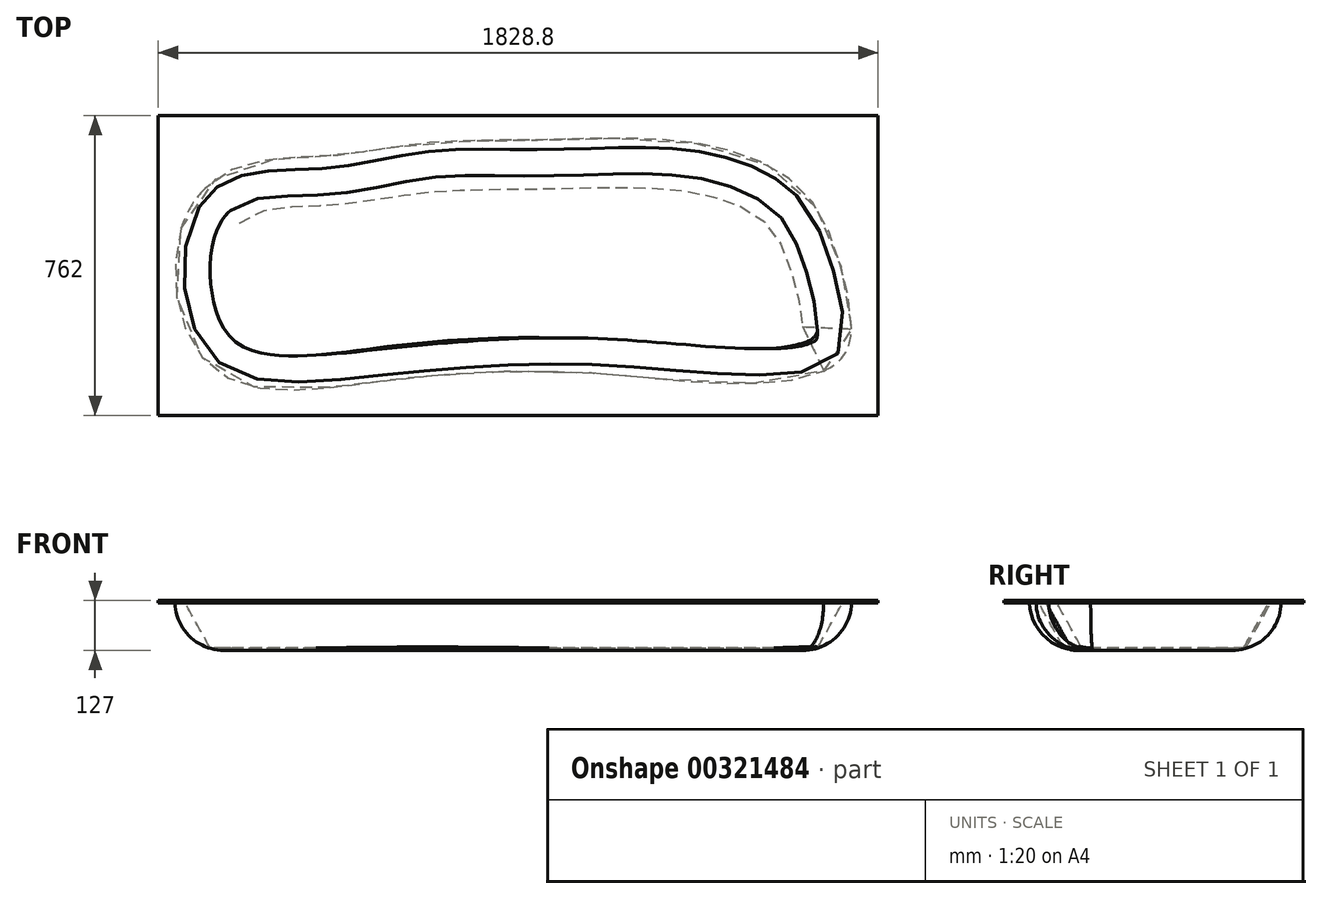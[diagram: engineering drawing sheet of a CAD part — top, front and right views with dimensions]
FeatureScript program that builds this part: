
annotation { "Feature Type Name" : "Feature", "Feature Type Description" : "" }
export const myFeature = defineFeature(function(context is Context, id is Id, definition is map)
    precondition{}
    {
        {
            var Q0;
            Q0=qCreatedBy(makeId("Top.planeOp"),FACE);
            var sketch = newSketch(context, id + "F0", { "sketchPlane" : qUnion([Q0])});
            skLineSegment(sketch, "E0.bottom", {"start": v(-1740.96, 737.08) * mm, "end": v(87.84, 737.08) * mm});
            skLineSegment(sketch, "E0.top", {"start": v(-1740.96, -24.92) * mm, "end": v(87.84, -24.92) * mm});
            skLineSegment(sketch, "E0.left", {"start": v(-1740.96, 737.08) * mm, "end": v(-1740.96, -24.92) * mm});
            skLineSegment(sketch, "E0.right", {"start": v(87.84, 737.08) * mm, "end": v(87.84, -24.92) * mm});
            skFitSpline(sketch, "E1", {"points": [v(-1683.24, 449.86) * mm, v(-1541.71, 604.65) * mm, v(-1298.47, 635.6) * mm, v(-1064.08, 666.57) * mm, v(-758.92, 675.41) * mm, v(-374.16, 666.57) * mm, v(-104.38, 547.16) * mm, v(0, 326.03) * mm, v(0, 127.01) * mm, v(-241.48, 56.25) * mm, v(-639.51, 82.79) * mm, v(-1112.73, 69.52) * mm, v(-1497.49, 47.4) * mm, v(-1661.12, 171.24) * mm, v(-1683.24, 449.86) * mm]});
            skFitSpline(sketch, "E2", {"points": [v(-1643.63, 182.8) * mm, v(-1661.97, 449.86) * mm, v(-1541.71, 580.79) * mm, v(-1297, 604.65) * mm, v(-1062.24, 644.98) * mm, v(-754.12, 650.48) * mm, v(-378.14, 646.81) * mm, v(-119.54, 533.1) * mm, v(-18.67, 314.85) * mm, v(-18.67, 127.01) * mm, v(-246.1, 78.26) * mm, v(-639.51, 103.94) * mm, v(-1120.93, 82.79) * mm, v(-1497.49, 69.1) * mm, v(-1643.63, 182.8) * mm]});
            skSolve(sketch);
        }
        {
            var Q0;
            Q0=makeQuery(id+"F0.imprint","IMPRINT",FACE,{"disambiguationData":[TD([[makeQuery(id+"F0.imprint","IMPRINT",EDGE,{"derivedFrom":sQuery(id+"F0.wireOp",EDGE,"E1")}),-1.0]])]});
            var Q1;
            Q1=makeQuery(id+"F0.imprint","IMPRINT",FACE,{"disambiguationData":[TD([[makeQuery(id+"F0.imprint","IMPRINT",EDGE,{"derivedFrom":sQuery(id+"F0.wireOp",EDGE,"E2")}),-1.0]])]});
            extrude(context, id + "F1", {"entities" : qUnion([Q0, Q1]), "oppositeDirection" : true, "depth" : 127 * mm});
        }
        {
            var Q0;
            Q0=makeQuery(id+"F1.opExtrude","CAP_EDGE",EDGE,{"disambiguationData":[OSD([sQuery(id+"F0.wireOp",EDGE,"E1")])],"isStart":false});
            fillet(context, id + "F2", {"entities" : qUnion([Q0]), "radius" : 124.46 * mm, "tangentPropagation" : true, "allowEdgeOverflow" : false});
        }
        {
            var Q0;
            Q0=makeQuery(id+"F0.imprint","IMPRINT",FACE,{"disambiguationData":[TD([[makeQuery(id+"F0.imprint","IMPRINT",EDGE,{"derivedFrom":sQuery(id+"F0.wireOp",EDGE,"E0.bottom")}),-1.0]])]});
            extrude(context, id + "F3", {"entities" : qUnion([Q0]), "operationType" : NewBodyOperationType.ADD, "oppositeDirection" : true, "depth" : 6.35 * mm});
        }
        {
            var Q0;
            Q0=makeQuery(id+"F0.imprint","IMPRINT",FACE,{"disambiguationData":[TD([[makeQuery(id+"F0.imprint","IMPRINT",EDGE,{"derivedFrom":sQuery(id+"F0.wireOp",EDGE,"E2")}),-1.0]])]});
            extrude(context, id + "F4", {"entities" : qUnion([Q0]), "operationType" : NewBodyOperationType.REMOVE, "oppositeDirection" : true, "depth" : 120.65 * mm, "hasDraft" : true, "draftAngle" : 29 * degree, "draftPullDirection" : true});
        }
    });
